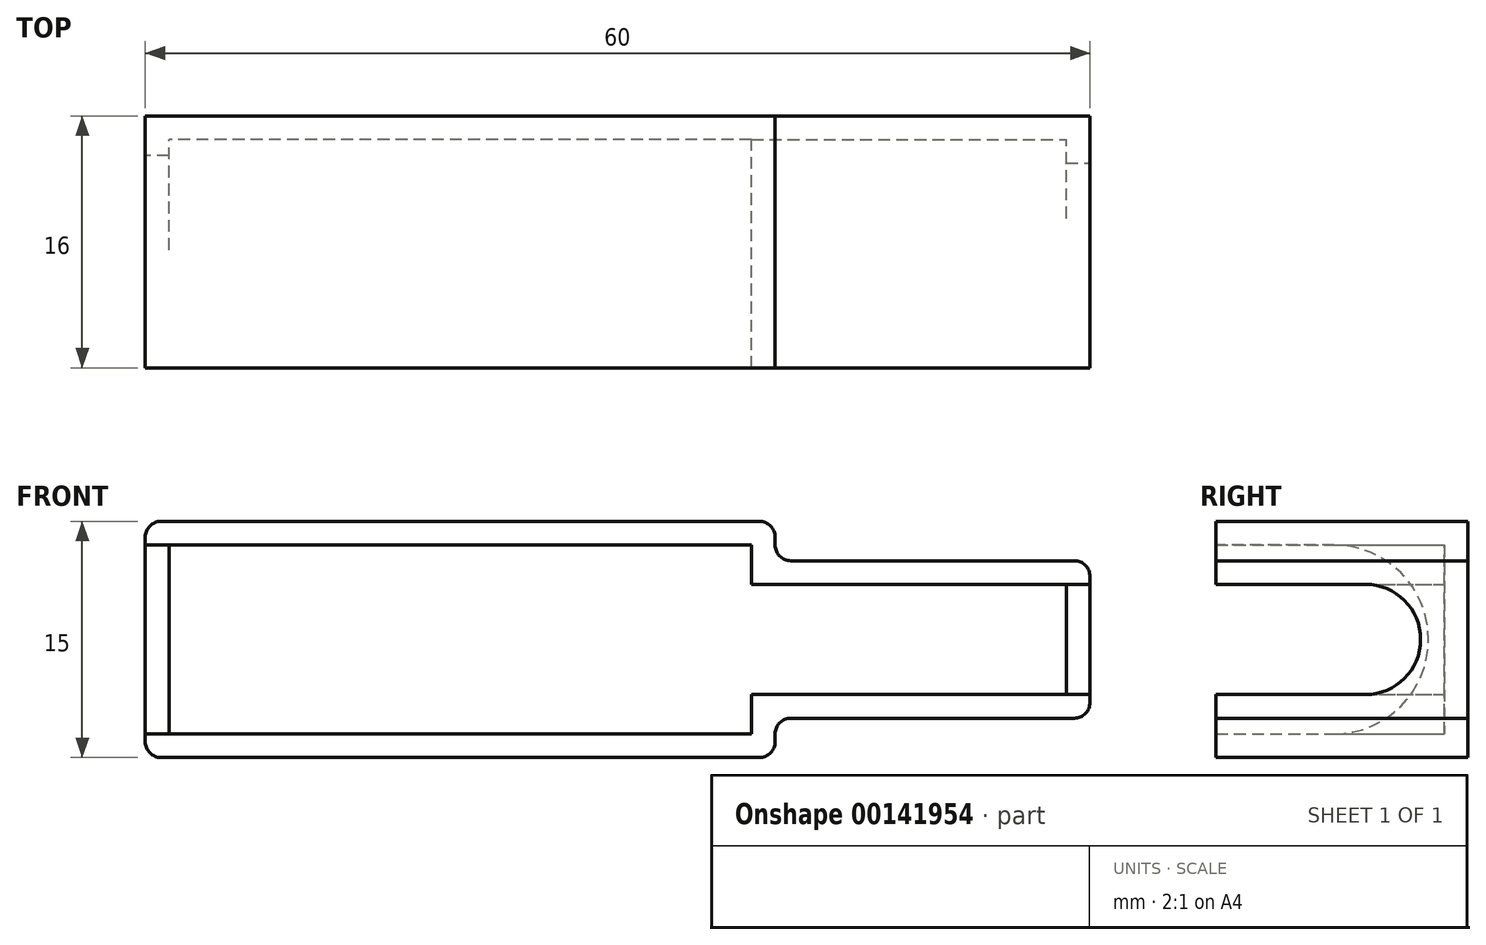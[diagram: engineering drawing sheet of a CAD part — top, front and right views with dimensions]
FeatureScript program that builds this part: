
annotation { "Feature Type Name" : "Feature", "Feature Type Description" : "" }
export const myFeature = defineFeature(function(context is Context, id is Id, definition is map)
    precondition{}
    {
        {
            var Q0;
            Q0=qCreatedBy(makeId("Front.planeOp"),FACE);
            var sketch = newSketch(context, id + "F0", { "sketchPlane" : qUnion([Q0])});
            skLineSegment(sketch, "E0", {"start": v(-30, 7.5) * mm, "end": v(-30, -7.5) * mm});
            skLineSegment(sketch, "E1", {"start": v(-30, -7.5) * mm, "end": v(10, -7.5) * mm});
            skLineSegment(sketch, "E2", {"start": v(10, -7.5) * mm, "end": v(10, -5) * mm});
            skLineSegment(sketch, "E3", {"start": v(10, -5) * mm, "end": v(30, -5) * mm});
            skLineSegment(sketch, "E4", {"start": v(30, -5) * mm, "end": v(30, 5) * mm});
            skLineSegment(sketch, "E5", {"start": v(30, 5) * mm, "end": v(10, 5) * mm});
            skLineSegment(sketch, "E6", {"start": v(10, 5) * mm, "end": v(10, 7.5) * mm});
            skLineSegment(sketch, "E7", {"start": v(10, 7.5) * mm, "end": v(-30, 7.5) * mm});
            skSolve(sketch);
        }
        {
            var Q0;
            Q0=makeQuery(id+"F0.imprint","IMPRINT",FACE,{"disambiguationData":[TD([[makeQuery(id+"F0.imprint","IMPRINT",EDGE,{"derivedFrom":sQuery(id+"F0.wireOp",EDGE,"E0")}),1.0]])]});
            extrude(context, id + "F1", {"entities" : qUnion([Q0]), "depth" : 16 * mm, "offsetDistance" : 25 * mm});
        }
        {
            var Q0;
            Q0=makeQuery(id+"F1.opExtrude","CAP_FACE",FACE,{"disambiguationData":[OSD([sQuery(id+"F0.wireOp",EDGE,"E0"),sQuery(id+"F0.wireOp",EDGE,"E1"),sQuery(id+"F0.wireOp",EDGE,"E2"),sQuery(id+"F0.wireOp",EDGE,"E3"),sQuery(id+"F0.wireOp",EDGE,"E4"),sQuery(id+"F0.wireOp",EDGE,"E5"),sQuery(id+"F0.wireOp",EDGE,"E6"),sQuery(id+"F0.wireOp",EDGE,"E7")])],"isStart":false});
            shell(context, id + "F2", {"entities" : qUnion([Q0]), "thickness" : 1.5 * mm});
        }
        {
            var Q0;
            Q0=makeQuery(id+"F1.opExtrude","SWEPT_FACE",FACE,{"disambiguationData":[OSD([sQuery(id+"F0.wireOp",EDGE,"E4")])]});
            var sketch = newSketch(context, id + "F3", { "sketchPlane" : qUnion([Q0])});
            skCircle(sketch, "E8", {"center": v(-6.5, 0) * mm, "radius": 3.5 * mm});
            skLineSegment(sketch, "E9", {"start": v(-6.5, -3.5) * mm, "end": v(-16, -3.5) * mm});
            skLineSegment(sketch, "E10", {"start": v(-16, -3.5) * mm, "end": v(-16, 3.5) * mm});
            skLineSegment(sketch, "E11", {"start": v(-16, 3.5) * mm, "end": v(-6.5, 3.5) * mm});
            skSolve(sketch);
        }
        {
            var Q0;
            {var subQ0=sQuery(id+"F3.wireOp",EDGE,"E9");Q0=makeQuery(id+"F3.imprint","IMPRINT",FACE,{"disambiguationData":[TD([[makeQuery(id+"F3.imprint","IMPRINT",EDGE,{"derivedFrom":subQ0}),-1.0]])]});}
            var Q1;
            {var subQ0=sQuery(id+"F3.wireOp",EDGE,"E8");var subQ1=makeQuery(id+"F3.imprint","INTERSECT",VERTEX,{"derivedFrom":[subQ0,sQuery(id+"F3.wireOp",EDGE,"E9")]});Q1=makeQuery(id+"F3.imprint","IMPRINT",FACE,{"disambiguationData":[TD([[makeQuery(id+"F3.imprint","IMPRINT",EDGE,{"disambiguationData":[TD([[subQ1,1.0]])],"derivedFrom":subQ0}),1.0]])]});}
            extrude(context, id + "F4", {"entities" : qUnion([Q0, Q1]), "operationType" : NewBodyOperationType.REMOVE, "oppositeDirection" : true, "depth" : 25 * mm, "offsetDistance" : 25 * mm});
        }
        {
            var Q0;
            Q0=makeQuery(id+"F1.opExtrude","SWEPT_FACE",FACE,{"disambiguationData":[OSD([sQuery(id+"F0.wireOp",EDGE,"E0")])]});
            var sketch = newSketch(context, id + "F5", { "sketchPlane" : qUnion([Q0])});
            skCircle(sketch, "E12", {"center": v(8.5, 0) * mm, "radius": 6 * mm});
            skLineSegment(sketch, "E13", {"start": v(8.5, 6) * mm, "end": v(16, 6) * mm});
            skLineSegment(sketch, "E14", {"start": v(16, 6) * mm, "end": v(16, -6) * mm});
            skLineSegment(sketch, "E15", {"start": v(16, -6) * mm, "end": v(8.5, -6) * mm});
            skSolve(sketch);
        }
        {
            var Q0;
            {var subQ0=sQuery(id+"F5.wireOp",EDGE,"E12");var subQ1=makeQuery(id+"F5.imprint","INTERSECT",VERTEX,{"derivedFrom":[subQ0,sQuery(id+"F5.wireOp",EDGE,"E13")]});Q0=makeQuery(id+"F5.imprint","IMPRINT",FACE,{"disambiguationData":[TD([[makeQuery(id+"F5.imprint","IMPRINT",EDGE,{"disambiguationData":[TD([[subQ1,-1.0]])],"derivedFrom":subQ0}),1.0]])]});}
            var Q1;
            {var subQ0=sQuery(id+"F5.wireOp",EDGE,"E13");Q1=makeQuery(id+"F5.imprint","IMPRINT",FACE,{"disambiguationData":[TD([[makeQuery(id+"F5.imprint","IMPRINT",EDGE,{"derivedFrom":subQ0}),-1.0]])]});}
            extrude(context, id + "F6", {"entities" : qUnion([Q0, Q1]), "operationType" : NewBodyOperationType.REMOVE, "oppositeDirection" : true, "depth" : 25 * mm, "offsetDistance" : 25 * mm});
        }
        {
            var Q0;
            Q0=makeQuery(id+"F1.opExtrude","SWEPT_EDGE",EDGE,{"disambiguationData":[OSD([sQuery(id+"F0.wireOp",EDGE,"E0"),sQuery(id+"F0.wireOp",EDGE,"E1")])]});
            var Q1;
            Q1=makeQuery(id+"F1.opExtrude","SWEPT_EDGE",EDGE,{"disambiguationData":[OSD([sQuery(id+"F0.wireOp",EDGE,"E0"),sQuery(id+"F0.wireOp",EDGE,"E7")])]});
            var Q2;
            Q2=makeQuery(id+"F1.opExtrude","SWEPT_EDGE",EDGE,{"disambiguationData":[OSD([sQuery(id+"F0.wireOp",EDGE,"E5"),sQuery(id+"F0.wireOp",EDGE,"E6")])]});
            var Q3;
            Q3=makeQuery(id+"F1.opExtrude","SWEPT_EDGE",EDGE,{"disambiguationData":[OSD([sQuery(id+"F0.wireOp",EDGE,"E6"),sQuery(id+"F0.wireOp",EDGE,"E7")])]});
            var Q4;
            Q4=makeQuery(id+"F1.opExtrude","SWEPT_EDGE",EDGE,{"disambiguationData":[OSD([sQuery(id+"F0.wireOp",EDGE,"E1"),sQuery(id+"F0.wireOp",EDGE,"E2")])]});
            var Q5;
            Q5=makeQuery(id+"F1.opExtrude","SWEPT_EDGE",EDGE,{"disambiguationData":[OSD([sQuery(id+"F0.wireOp",EDGE,"E2"),sQuery(id+"F0.wireOp",EDGE,"E3")])]});
            var Q6;
            Q6=makeQuery(id+"F1.opExtrude","SWEPT_EDGE",EDGE,{"disambiguationData":[OSD([sQuery(id+"F0.wireOp",EDGE,"E3"),sQuery(id+"F0.wireOp",EDGE,"E4")])]});
            var Q7;
            Q7=makeQuery(id+"F1.opExtrude","SWEPT_EDGE",EDGE,{"disambiguationData":[OSD([sQuery(id+"F0.wireOp",EDGE,"E4"),sQuery(id+"F0.wireOp",EDGE,"E5")])]});
            fillet(context, id + "F7", {"entities" : qUnion([Q0, Q1, Q2, Q3, Q4, Q5, Q6, Q7]), "radius" : 1 * mm, "tangentPropagation" : true, "allowEdgeOverflow" : false});
        }
    });
